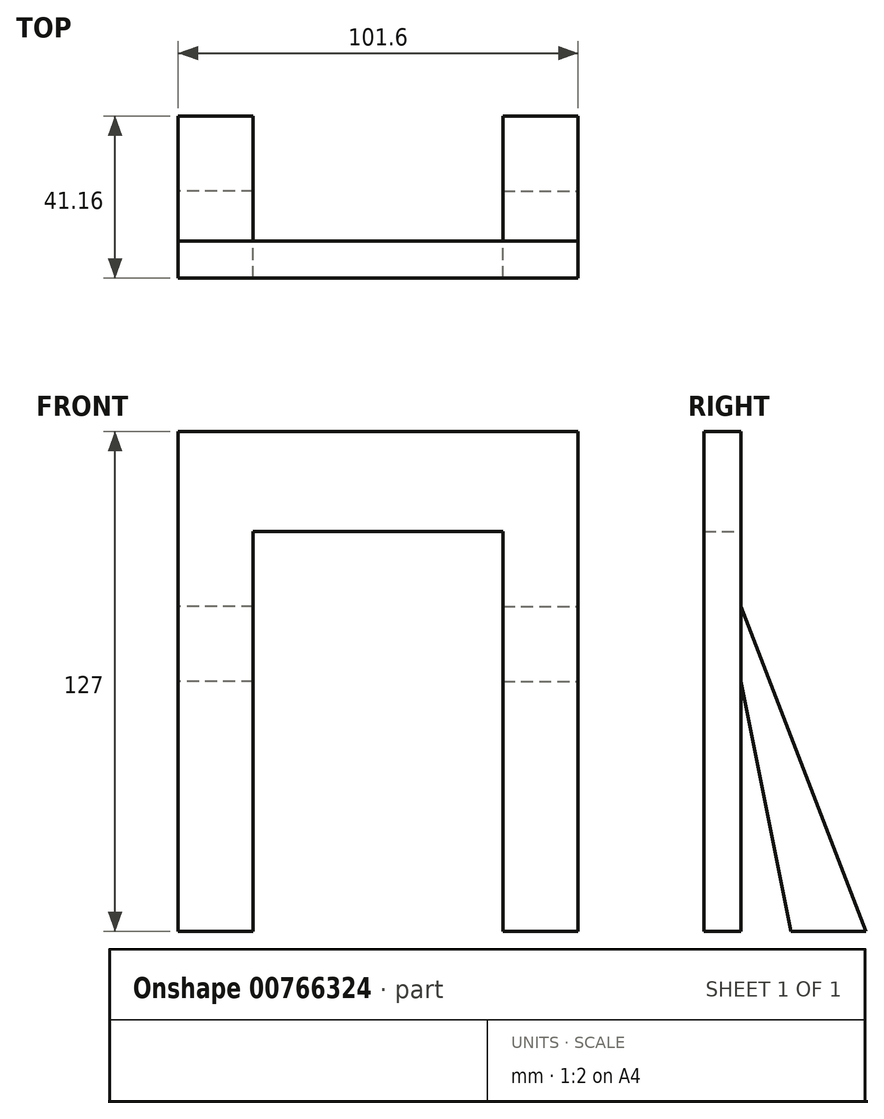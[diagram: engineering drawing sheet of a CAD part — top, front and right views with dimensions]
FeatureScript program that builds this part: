
annotation { "Feature Type Name" : "Feature", "Feature Type Description" : "" }
export const myFeature = defineFeature(function(context is Context, id is Id, definition is map)
    precondition{}
    {
        {
            var Q0;
            Q0=qCreatedBy(makeId("Front.planeOp"),FACE);
            var sketch = newSketch(context, id + "F0", { "sketchPlane" : qUnion([Q0])});
            skLineSegment(sketch, "E0.bottom", {"start": v(-47.17, 127) * mm, "end": v(54.43, 127) * mm});
            skLineSegment(sketch, "E0.top", {"start": v(-47.17, 101.6) * mm, "end": v(54.43, 101.6) * mm});
            skLineSegment(sketch, "E0.left", {"start": v(-47.17, 127) * mm, "end": v(-47.17, 101.6) * mm});
            skLineSegment(sketch, "E0.right", {"start": v(54.43, 127) * mm, "end": v(54.43, 101.6) * mm});
            skLineSegment(sketch, "E1.bottom", {"start": v(-47.17, 127) * mm, "end": v(-28.12, 127) * mm});
            skLineSegment(sketch, "E1.top", {"start": v(-47.17, 0) * mm, "end": v(-28.12, 0) * mm});
            skLineSegment(sketch, "E1.left", {"start": v(-47.17, 127) * mm, "end": v(-47.17, 0) * mm});
            skLineSegment(sketch, "E1.right", {"start": v(-28.12, 127) * mm, "end": v(-28.12, 0) * mm});
            skLineSegment(sketch, "E2.bottom", {"start": v(54.43, 127) * mm, "end": v(35.38, 127) * mm});
            skLineSegment(sketch, "E2.top", {"start": v(54.43, 0) * mm, "end": v(35.38, 0) * mm});
            skLineSegment(sketch, "E2.left", {"start": v(54.43, 127) * mm, "end": v(54.43, 0) * mm});
            skLineSegment(sketch, "E2.right", {"start": v(35.38, 127) * mm, "end": v(35.38, 0) * mm});
            skLineSegment(sketch, "E3.bottom", {"start": v(-28.12, 82.55) * mm, "end": v(-47.17, 82.55) * mm});
            skLineSegment(sketch, "E3.top", {"start": v(-28.12, 63.5) * mm, "end": v(-47.17, 63.5) * mm});
            skLineSegment(sketch, "E3.left", {"start": v(-28.12, 82.55) * mm, "end": v(-28.12, 63.5) * mm});
            skLineSegment(sketch, "E3.right", {"start": v(-47.17, 82.55) * mm, "end": v(-47.17, 63.5) * mm});
            skLineSegment(sketch, "E4.bottom", {"start": v(35.38, 82.55) * mm, "end": v(54.43, 82.55) * mm});
            skLineSegment(sketch, "E4.top", {"start": v(35.38, 63.5) * mm, "end": v(54.43, 63.5) * mm});
            skLineSegment(sketch, "E4.left", {"start": v(35.38, 82.55) * mm, "end": v(35.38, 63.5) * mm});
            skLineSegment(sketch, "E4.right", {"start": v(54.43, 82.55) * mm, "end": v(54.43, 63.5) * mm});
            skSolve(sketch);
        }
        {
            var Q0;
            Q0=qCreatedBy(makeId("Top.planeOp"),FACE);
            var sketch = newSketch(context, id + "F1", { "sketchPlane" : qUnion([Q0])});
            skLineSegment(sketch, "E5.bottom", {"start": v(35.38, 12.7) * mm, "end": v(54.43, 12.7) * mm});
            skLineSegment(sketch, "E5.top", {"start": v(35.38, 31.75) * mm, "end": v(54.43, 31.75) * mm});
            skLineSegment(sketch, "E5.left", {"start": v(35.38, -1.7) * mm, "end": v(35.38, 31.75) * mm});
            skLineSegment(sketch, "E5.right", {"start": v(54.43, -2.04) * mm, "end": v(54.43, 31.75) * mm});
            skLineSegment(sketch, "E6.bottom", {"start": v(-28.12, 12.7) * mm, "end": v(-47.17, 12.7) * mm});
            skLineSegment(sketch, "E6.top", {"start": v(-28.12, 31.75) * mm, "end": v(-47.17, 31.75) * mm});
            skLineSegment(sketch, "E6.left", {"start": v(-28.12, -4.26) * mm, "end": v(-28.12, 31.75) * mm});
            skLineSegment(sketch, "E6.right", {"start": v(-47.17, -3.47) * mm, "end": v(-47.17, 31.75) * mm});
            skSolve(sketch);
        }
        {
            var Q0;
            {var subQ0=sQuery(id+"F1.wireOp",EDGE,"E5.bottom");Q0=makeQuery(id+"F1.imprint","IMPRINT",FACE,{"disambiguationData":[TD([[makeQuery(id+"F1.imprint","IMPRINT",EDGE,{"derivedFrom":subQ0}),1.0]])]});}
            var Q1;
            Q1=makeQuery(id+"F0.imprint","IMPRINT",FACE,{"disambiguationData":[TD([[makeQuery(id+"F0.imprint","IMPRINT",EDGE,{"derivedFrom":sQuery(id+"F0.wireOp",EDGE,"E4.bottom")}),-1.0]])]});
            loft(context, id + "F2", {"sheetProfilesArray" : [{ "sheetProfileEntities" : qUnion([Q0]) }, { "sheetProfileEntities" : qUnion([Q1]) }]});
        }
        {
            var Q0;
            {var subQ0=sQuery(id+"F1.wireOp",EDGE,"E6.bottom");Q0=makeQuery(id+"F1.imprint","IMPRINT",FACE,{"disambiguationData":[TD([[makeQuery(id+"F1.imprint","IMPRINT",EDGE,{"derivedFrom":subQ0}),-1.0]])]});}
            var Q1;
            Q1=makeQuery(id+"F0.imprint","IMPRINT",FACE,{"disambiguationData":[TD([[makeQuery(id+"F0.imprint","IMPRINT",EDGE,{"derivedFrom":sQuery(id+"F0.wireOp",EDGE,"E3.bottom")}),1.0]])]});
            loft(context, id + "F3", {"sheetProfilesArray" : [{ "sheetProfileEntities" : qUnion([Q0]) }, { "sheetProfileEntities" : qUnion([Q1]) }]});
        }
        {
            var Q0;
            {var subQ5=sQuery(id+"F0.wireOp",EDGE,"E3.bottom");Q0=makeQuery(id+"F0.imprint","IMPRINT",FACE,{"disambiguationData":[TD([[makeQuery(id+"F0.imprint","IMPRINT",EDGE,{"derivedFrom":subQ5}),-1.0]])]});}
            var Q1;
            {var subQ5=sQuery(id+"F0.wireOp",EDGE,"E1.bottom");Q1=makeQuery(id+"F0.imprint","IMPRINT",FACE,{"disambiguationData":[TD([[makeQuery(id+"F0.imprint","IMPRINT",EDGE,{"derivedFrom":subQ5}),-1.0]])]});}
            var Q2;
            {var subQ0=sQuery(id+"F0.wireOp",EDGE,"E0.bottom");Q2=makeQuery(id+"F0.imprint","IMPRINT",FACE,{"disambiguationData":[TD([[makeQuery(id+"F0.imprint","IMPRINT",EDGE,{"derivedFrom":subQ0}),-1.0]])]});}
            var Q3;
            {var subQ5=sQuery(id+"F0.wireOp",EDGE,"E2.bottom");Q3=makeQuery(id+"F0.imprint","IMPRINT",FACE,{"disambiguationData":[TD([[makeQuery(id+"F0.imprint","IMPRINT",EDGE,{"derivedFrom":subQ5}),1.0]])]});}
            var Q4;
            {var subQ5=sQuery(id+"F0.wireOp",EDGE,"E4.bottom");Q4=makeQuery(id+"F0.imprint","IMPRINT",FACE,{"disambiguationData":[TD([[makeQuery(id+"F0.imprint","IMPRINT",EDGE,{"derivedFrom":subQ5}),1.0]])]});}
            var Q5;
            {var subQ0=sQuery(id+"F0.wireOp",EDGE,"E1.top");Q5=makeQuery(id+"F0.imprint","IMPRINT",FACE,{"disambiguationData":[TD([[makeQuery(id+"F0.imprint","IMPRINT",EDGE,{"derivedFrom":subQ0}),1.0]])]});}
            var Q6;
            Q6=makeQuery(id+"F0.imprint","IMPRINT",FACE,{"disambiguationData":[TD([[makeQuery(id+"F0.imprint","IMPRINT",EDGE,{"derivedFrom":sQuery(id+"F0.wireOp",EDGE,"E3.bottom")}),1.0]])]});
            var Q7;
            {var subQ0=sQuery(id+"F0.wireOp",EDGE,"E2.top");Q7=makeQuery(id+"F0.imprint","IMPRINT",FACE,{"disambiguationData":[TD([[makeQuery(id+"F0.imprint","IMPRINT",EDGE,{"derivedFrom":subQ0}),-1.0]])]});}
            var Q8;
            Q8=makeQuery(id+"F0.imprint","IMPRINT",FACE,{"disambiguationData":[TD([[makeQuery(id+"F0.imprint","IMPRINT",EDGE,{"derivedFrom":sQuery(id+"F0.wireOp",EDGE,"E4.bottom")}),-1.0]])]});
            extrude(context, id + "F4", {"entities" : qUnion([Q0, Q1, Q2, Q3, Q4, Q5, Q6, Q7, Q8]), "depth" : 9.4 * mm, "offsetDistance" : 25.4 * mm});
        }
    });
